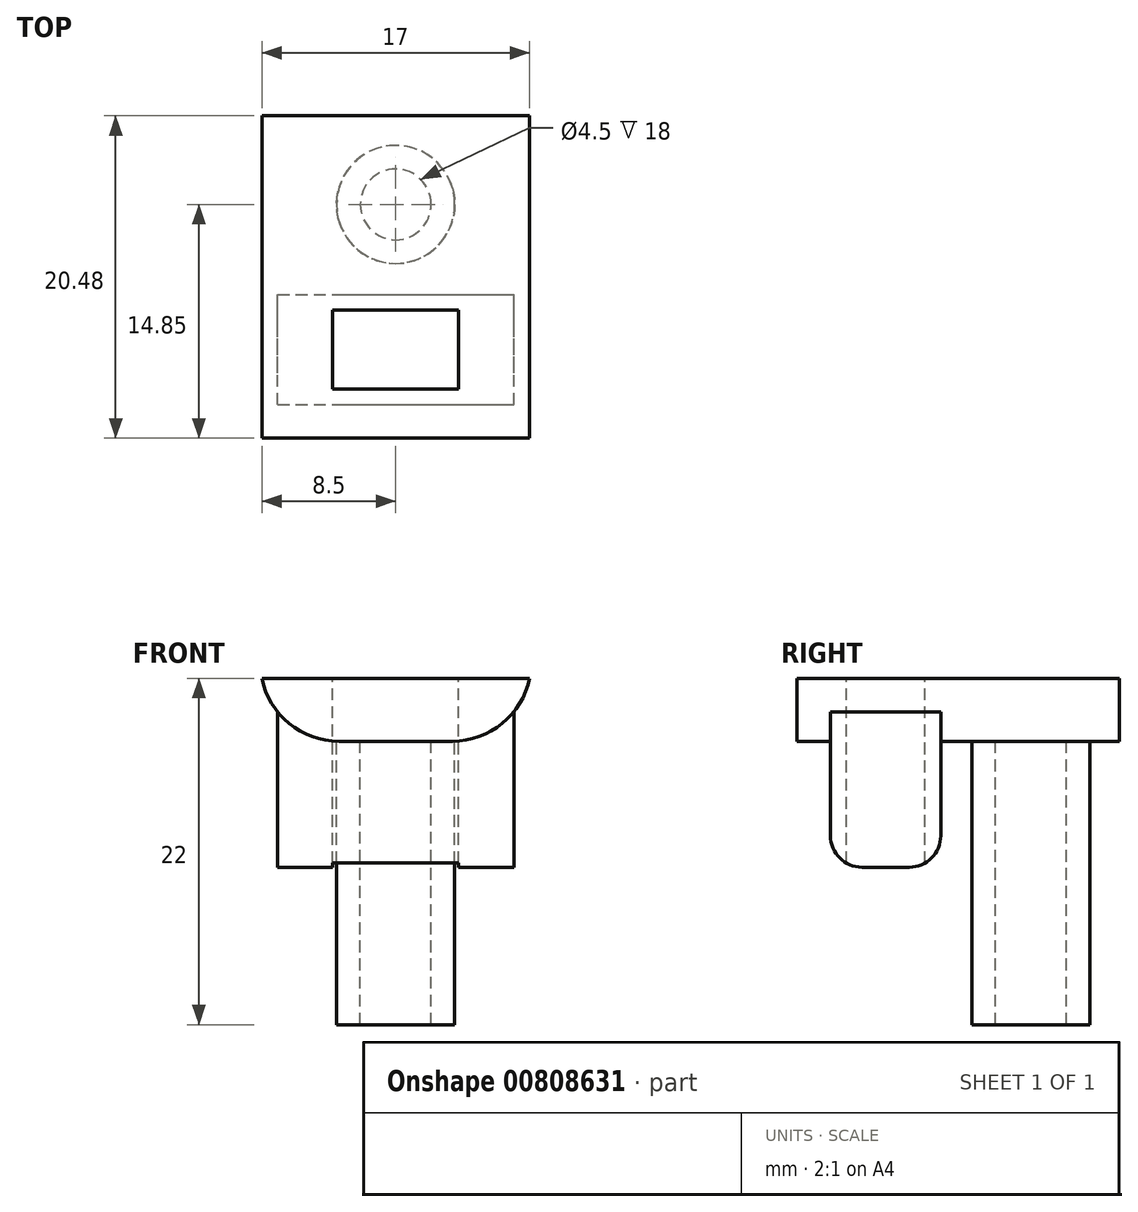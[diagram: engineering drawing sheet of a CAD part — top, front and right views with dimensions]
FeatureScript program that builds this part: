
annotation { "Feature Type Name" : "Feature", "Feature Type Description" : "" }
export const myFeature = defineFeature(function(context is Context, id is Id, definition is map)
    precondition{}
    {
        {
            var Q0;
            Q0=qCreatedBy(makeId("Top.planeOp"),FACE);
            var sketch = newSketch(context, id + "F0", { "sketchPlane" : qUnion([Q0])});
            skCircle(sketch, "E0", {"center": v(0, 0) * mm, "radius": 2.25 * mm});
            skCircle(sketch, "E1", {"center": v(0, 0) * mm, "radius": 3.75 * mm});
            skLineSegment(sketch, "E2.bottom", {"start": v(-4, -11.72) * mm, "end": v(4, -11.72) * mm});
            skLineSegment(sketch, "E2.top", {"start": v(-4, -6.72) * mm, "end": v(4, -6.72) * mm});
            skLineSegment(sketch, "E2.left", {"start": v(-4, -11.72) * mm, "end": v(-4, -6.72) * mm});
            skLineSegment(sketch, "E2.right", {"start": v(4, -11.72) * mm, "end": v(4, -6.72) * mm});
            skPoint(sketch, "E2.middle", {"position": v(0, -9.22) * mm});
            skLineSegment(sketch, "E3.bottom", {"start": v(-7.5, -12.72) * mm, "end": v(7.5, -12.72) * mm});
            skLineSegment(sketch, "E3.top", {"start": v(-7.5, -5.72) * mm, "end": v(7.5, -5.72) * mm});
            skLineSegment(sketch, "E3.left", {"start": v(-7.5, -12.72) * mm, "end": v(-7.5, -5.72) * mm});
            skLineSegment(sketch, "E3.right", {"start": v(7.5, -12.72) * mm, "end": v(7.5, -5.72) * mm});
            skLineSegment(sketch, "E4", {"start": v(0, 0) * mm, "end": v(0, -9.22) * mm});
            skSolve(sketch);
        }
        {
            var Q0;
            Q0=qCreatedBy(makeId("Top.planeOp"),FACE);
            var sketch = newSketch(context, id + "F1", { "sketchPlane" : qUnion([Q0])});
            skLineSegment(sketch, "E5.bottom", {"start": v(8.5, 5.63) * mm, "end": v(-8.5, 5.63) * mm});
            skLineSegment(sketch, "E5.top", {"start": v(8.5, -14.85) * mm, "end": v(-8.5, -14.85) * mm});
            skLineSegment(sketch, "E5.left", {"start": v(8.5, 5.63) * mm, "end": v(8.5, -14.85) * mm});
            skLineSegment(sketch, "E5.right", {"start": v(-8.5, 5.63) * mm, "end": v(-8.5, -14.85) * mm});
            skLineSegment(sketch, "E6", {"start": v(0, 5.63) * mm, "end": v(0, -14.85) * mm});
            skSolve(sketch);
        }
        {
            var Q0;
            Q0 = qSketchRegion(id + "F1", true);
            extrude(context, id + "F2", {"entities" : qUnion([Q0]), "depth" : -4 * mm, "offsetDistance" : 25 * mm});
        }
        {
            var Q0;
            Q0 = qSketchRegion(id + "F0", true);
            extrude(context, id + "F3", {"entities" : qUnion([Q0]), "operationType" : NewBodyOperationType.ADD, "depth" : -12 * mm, "offsetDistance" : 25 * mm});
        }
        {
            var Q0;
            Q0=makeQuery(id+"F3.boolean.opBoolean","SPLIT",FACE,{"disambiguationData":[TD([makeQuery(id+"F3.opExtrude","SWEPT_FACE",FACE,{"disambiguationData":[OSD([sQuery(id+"F0.wireOp",EDGE,"E2.bottom")])]})])],"derivedFrom":makeQuery(id+"F2.opExtrude","CAP_FACE",FACE,{"disambiguationData":[OSD([sQuery(id+"F1.wireOp",EDGE,"E5.bottom"),sQuery(id+"F1.wireOp",EDGE,"E5.top"),sQuery(id+"F1.wireOp",EDGE,"E5.left"),sQuery(id+"F1.wireOp",EDGE,"E5.right")])],"isStart":false})});
            extrude(context, id + "F4", {"entities" : qUnion([Q0]), "operationType" : NewBodyOperationType.REMOVE, "oppositeDirection" : true, "depth" : 4 * mm, "offsetDistance" : 25 * mm});
        }
        {
            var Q0;
            Q0=makeQuery(id+"F3.opExtrude","CAP_FACE",FACE,{"disambiguationData":[OSD([sQuery(id+"F0.wireOp",EDGE,"E0"),sQuery(id+"F0.wireOp",EDGE,"E1")])],"isStart":false});
            extrude(context, id + "F5", {"entities" : qUnion([Q0]), "operationType" : NewBodyOperationType.ADD, "depth" : 10 * mm, "offsetDistance" : 25 * mm});
        }
        {
            var Q0;
            Q0=makeQuery(id+"F3.opExtrude","CAP_EDGE",EDGE,{"disambiguationData":[OSD([sQuery(id+"F0.wireOp",EDGE,"E3.bottom")])],"isStart":false});
            var Q1;
            Q1=makeQuery(id+"F3.opExtrude","CAP_EDGE",EDGE,{"disambiguationData":[OSD([sQuery(id+"F0.wireOp",EDGE,"E3.top")])],"isStart":false});
            fillet(context, id + "F6", {"entities" : qUnion([Q0, Q1]), "radius" : 2 * mm, "tangentPropagation" : true, "allowEdgeOverflow" : false});
        }
        {
            var Q0;
            Q0=makeQuery(id+"F2.opExtrude","CAP_EDGE",EDGE,{"disambiguationData":[OSD([sQuery(id+"F1.wireOp",EDGE,"E5.right")])],"isStart":false});
            var Q1;
            Q1=makeQuery(id+"F2.opExtrude","CAP_EDGE",EDGE,{"disambiguationData":[OSD([sQuery(id+"F1.wireOp",EDGE,"E5.left")])],"isStart":false});
            fillet(context, id + "F7", {"entities" : qUnion([Q0, Q1]), "radius" : 5 * mm, "tangentPropagation" : true, "allowEdgeOverflow" : false});
        }
    });
